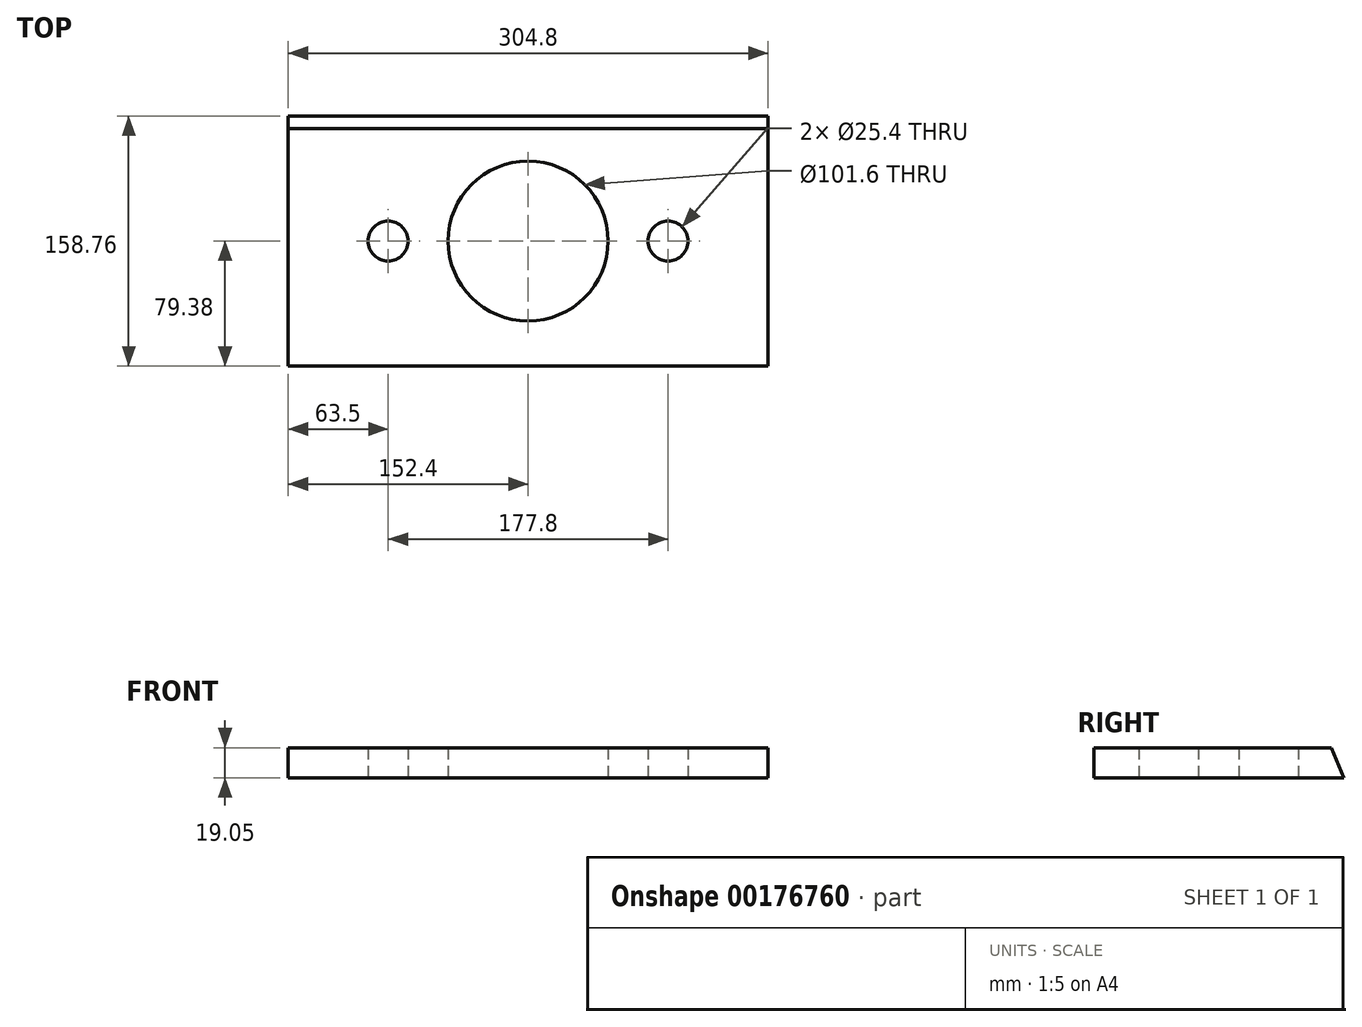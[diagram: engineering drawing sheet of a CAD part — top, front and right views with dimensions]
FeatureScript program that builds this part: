
annotation { "Feature Type Name" : "Feature", "Feature Type Description" : "" }
export const myFeature = defineFeature(function(context is Context, id is Id, definition is map)
    precondition{}
    {
        {
            var Q0;
            Q0=qCreatedBy(makeId("Top.planeOp"),FACE);
            var sketch = newSketch(context, id + "F0", { "sketchPlane" : qUnion([Q0])});
            skLineSegment(sketch, "E0.bottom", {"start": v(-152.4, 79.38) * mm, "end": v(152.4, 79.38) * mm});
            skLineSegment(sketch, "E0.top", {"start": v(-152.4, -79.37) * mm, "end": v(152.4, -79.37) * mm});
            skLineSegment(sketch, "E0.left", {"start": v(-152.4, 79.37) * mm, "end": v(-152.4, -79.37) * mm});
            skLineSegment(sketch, "E0.right", {"start": v(152.4, 79.37) * mm, "end": v(152.4, -79.37) * mm});
            skPoint(sketch, "E0.middle", {"position": v(0, 0) * mm});
            skCircle(sketch, "E1", {"center": v(0, 0) * mm, "radius": 50.8 * mm});
            skCircle(sketch, "E2", {"center": v(-88.9, 0) * mm, "radius": 12.7 * mm});
            skCircle(sketch, "E3.MirrorC", {"center": v(88.9, 0) * mm, "radius": 12.7 * mm});
            skPoint(sketch, "E4.orphan", {"position": v(-88.9, -40.74) * mm});
            skPoint(sketch, "E5.orphan", {"position": v(-88.9, 40.74) * mm});
            skLineSegment(sketch, "E6.trimOffspring", {"start": v(88.9, -12.7) * mm, "end": v(88.9, -40.74) * mm});
            skPoint(sketch, "E7.bottom.end.orphan", {"position": v(88.9, 40.74) * mm});
            skSolve(sketch);
        }
        {
            var Q0;
            Q0=makeQuery(id+"F0.imprint","IMPRINT",FACE,{"disambiguationData":[TD([[makeQuery(id+"F0.imprint","IMPRINT",EDGE,{"derivedFrom":sQuery(id+"F0.wireOp",EDGE,"E0.bottom")}),-1.0]])]});
            extrude(context, id + "F1", {"entities" : qUnion([Q0]), "depth" : 19.05 * mm});
        }
        {
            var Q0;
            Q0=makeQuery(id+"F1.opExtrude","CAP_EDGE",EDGE,{"disambiguationData":[OSD([sQuery(id+"F0.wireOp",EDGE,"E0.bottom")])],"isStart":false});
            chamfer(context, id + "F2", {"entities" : qUnion([Q0]), "chamferType" : ChamferType.OFFSET_ANGLE, "width" : 19.05 * mm, "oppositeDirection" : false, "angle" : 22.5 * degree, "tangentPropagation" : true});
        }
    });
